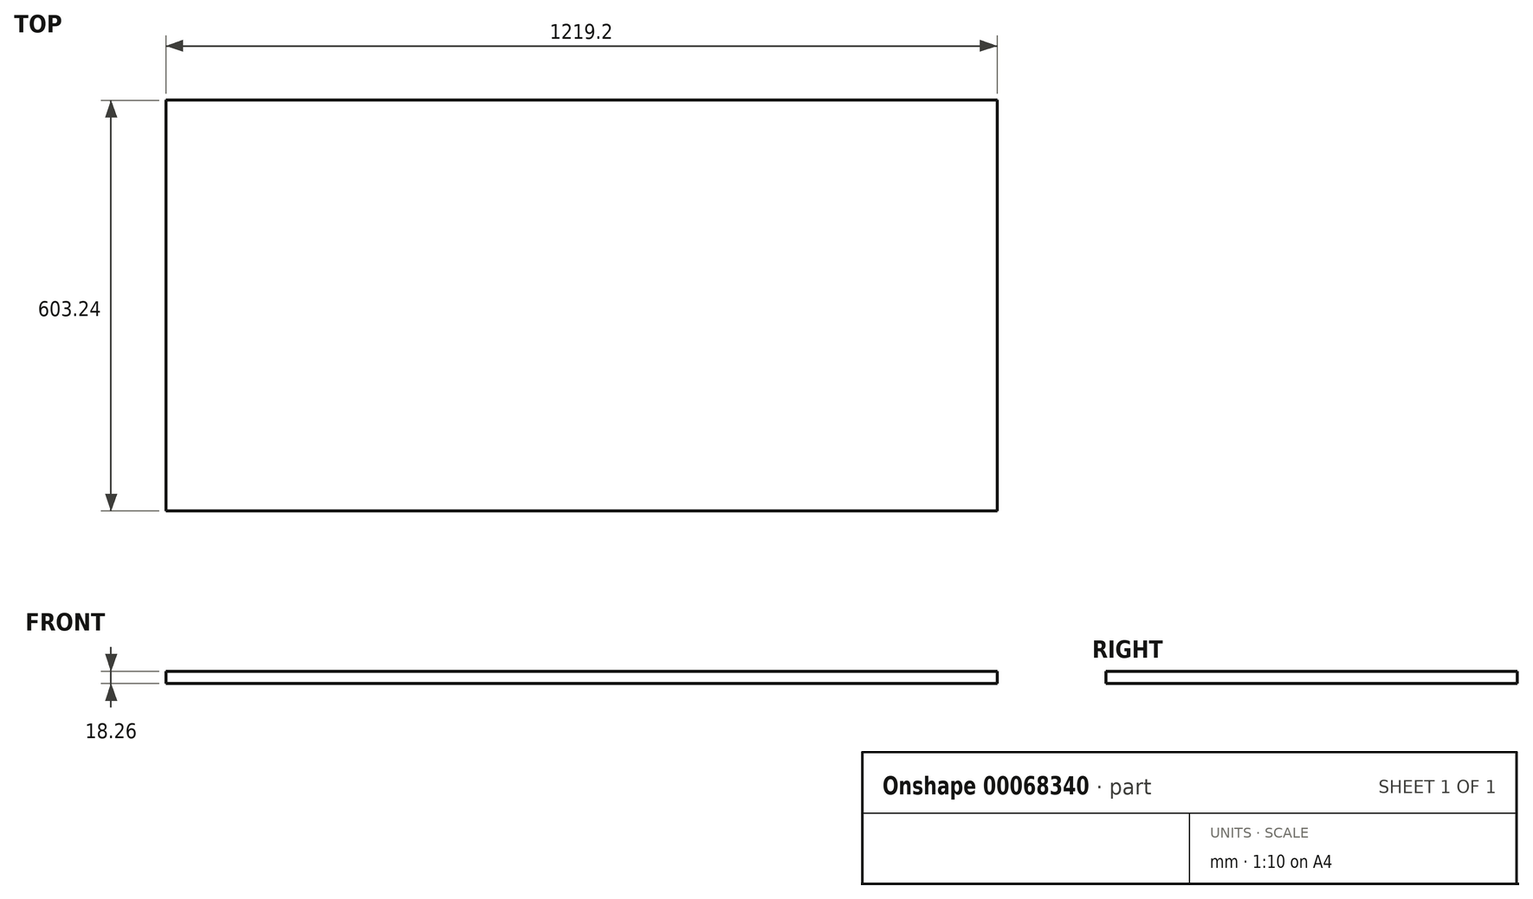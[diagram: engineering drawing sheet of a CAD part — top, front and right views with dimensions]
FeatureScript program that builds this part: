
annotation { "Feature Type Name" : "Feature", "Feature Type Description" : "" }
export const myFeature = defineFeature(function(context is Context, id is Id, definition is map)
    precondition{}
    {
        {
            var Q0;
            Q0=qCreatedBy(makeId("Right.planeOp"),FACE);
            var sketch = newSketch(context, id + "F0", { "sketchPlane" : qUnion([Q0])});
            skLineSegment(sketch, "E0.bottom", {"start": v(-301.63, 0) * mm, "end": v(301.63, 0) * mm});
            skLineSegment(sketch, "E0.top", {"start": v(-301.63, -18.26) * mm, "end": v(301.63, -18.26) * mm});
            skLineSegment(sketch, "E0.left", {"start": v(-301.63, 0) * mm, "end": v(-301.63, -18.26) * mm});
            skLineSegment(sketch, "E0.right", {"start": v(301.63, 0) * mm, "end": v(301.63, -18.26) * mm});
            skLineSegment(sketch, "E1.bottom", {"start": v(-253.87, 0) * mm, "end": v(-215.77, 0) * mm});
            skLineSegment(sketch, "E1.top", {"start": v(-253.87, 63.5) * mm, "end": v(-215.77, 63.5) * mm});
            skLineSegment(sketch, "E1.left", {"start": v(-253.87, 0) * mm, "end": v(-253.87, 63.5) * mm});
            skLineSegment(sketch, "E1.right", {"start": v(-215.77, 0) * mm, "end": v(-215.77, 63.5) * mm});
            skLineSegment(sketch, "E2.bottom", {"start": v(253.87, 0) * mm, "end": v(215.77, 0) * mm});
            skLineSegment(sketch, "E2.top", {"start": v(253.87, 63.5) * mm, "end": v(215.77, 63.5) * mm});
            skLineSegment(sketch, "E2.left", {"start": v(253.87, 0) * mm, "end": v(253.87, 63.5) * mm});
            skLineSegment(sketch, "E2.right", {"start": v(215.77, 0) * mm, "end": v(215.77, 63.5) * mm});
            skSolve(sketch);
        }
        {
            var Q0;
            Q0=makeQuery(id+"F0.imprint","IMPRINT",FACE,{"disambiguationData":[TD([[makeQuery(id+"F0.imprint","IMPRINT",EDGE,{"derivedFrom":sQuery(id+"F0.wireOp",EDGE,"E1.bottom")}),1.0]])]});
            var Q1;
            Q1=makeQuery(id+"F0.imprint","IMPRINT",FACE,{"disambiguationData":[TD([[makeQuery(id+"F0.imprint","IMPRINT",EDGE,{"derivedFrom":sQuery(id+"F0.wireOp",EDGE,"E0.top")}),1.0]])]});
            var Q2;
            Q2=makeQuery(id+"F0.imprint","IMPRINT",FACE,{"disambiguationData":[TD([[makeQuery(id+"F0.imprint","IMPRINT",EDGE,{"derivedFrom":sQuery(id+"F0.wireOp",EDGE,"E2.bottom")}),-1.0]])]});
            extrude(context, id + "F1", {"entities" : qUnion([Q0, Q1, Q2]), "endBound" : BoundingType.SYMMETRIC, "depth" : 1219.2 * mm});
        }
    });
